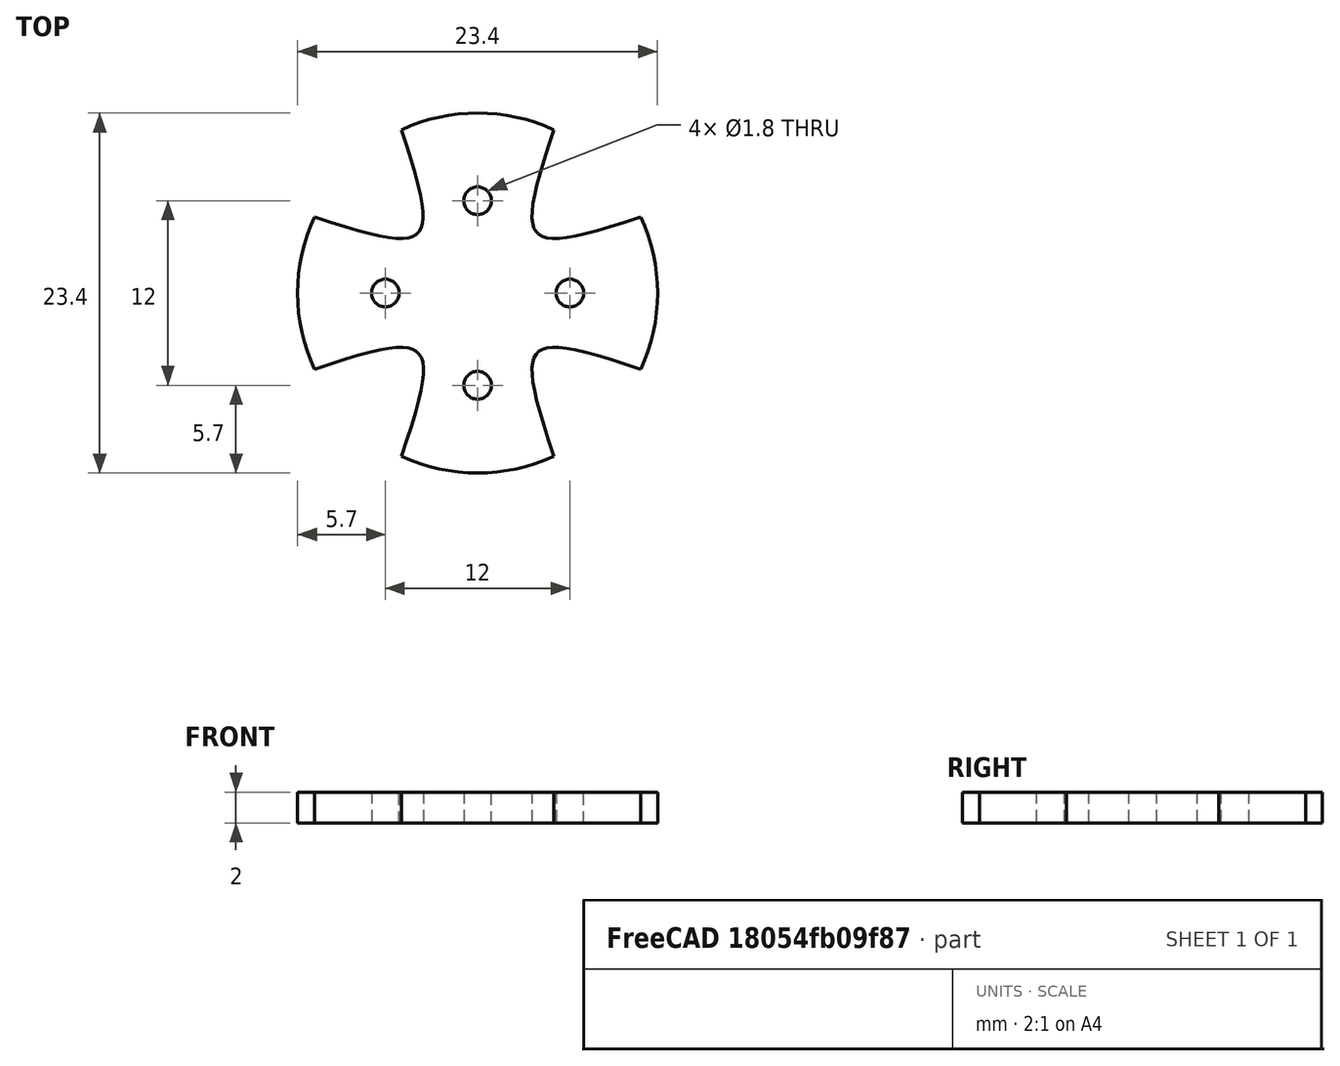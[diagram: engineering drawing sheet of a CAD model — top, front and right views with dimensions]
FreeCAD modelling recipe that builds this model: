
FCSTD DOCUMENT  (FreeCAD 0.19R0.19.2)
Label: boatMoterHolder011
License: All rights reserved
LicenseURL: http://en.wikipedia.org/wiki/All_rights_reserved
objects: Sketcher::SketchObject×2, Part::Extrusion×1
note: 3 computed .brp shape members not serialized (recipe doc carries the construction recipe); baked Part::Feature solids carry a one-line shape summary decoded from their .brp

FEATURE [Sketcher::SketchObject] Sketch
  FullyConstrained = true
  sketch-geometry (44):
    g0: Circle CenterX=-6 CenterY=0 CenterZ=0 NormalX=0 NormalY=0 NormalZ=1 AngleXU=0 Radius=0.9
    g1: Circle CenterX=0 CenterY=6 CenterZ=0 NormalX=0 NormalY=0 NormalZ=1 AngleXU=0 Radius=0.9
    g2: Circle CenterX=6 CenterY=0 CenterZ=0 NormalX=0 NormalY=0 NormalZ=1 AngleXU=0 Radius=0.9
    g3: Circle CenterX=0 CenterY=-6 CenterZ=0 NormalX=0 NormalY=0 NormalZ=1 AngleXU=0 Radius=0.9
    g4-g8: Circle x5 (B-spline internal-alignment scaffolding for g9; pole/knot coordinates omitted)
    g9: BSplineCurve PolesCount=5 KnotsCount=3 Degree=3 IsPeriodic=0
    g10: GeomPoint X=-4.94974 Y=10.6066 Z=0
    g11: GeomPoint X=-3.88908 Y=3.88909 Z=0
    g12: GeomPoint X=-10.6066 Y=4.94975 Z=0
    g13-g17: Circle x5 (B-spline internal-alignment scaffolding for g18; pole/knot coordinates omitted)
    g18: BSplineCurve PolesCount=5 KnotsCount=3 Degree=3 IsPeriodic=0
    g19: GeomPoint X=-10.6066 Y=-4.94974 Z=0
    g20: GeomPoint X=-3.88212 Y=-3.88197 Z=0
    g21: GeomPoint X=-4.94053 Y=-10.6109 Z=0
    g22-g26: Circle x5 (B-spline internal-alignment scaffolding for g27; pole/knot coordinates omitted)
    g27: BSplineCurve PolesCount=5 KnotsCount=3 Degree=3 IsPeriodic=0
    g28: GeomPoint X=4.94975 Y=-10.6066 Z=0
    g29: GeomPoint X=3.8852 Y=-3.88525 Z=0
    g30: GeomPoint X=10.603 Y=-4.95737 Z=0
    g31-g35: Circle x5 (B-spline internal-alignment scaffolding for g36; pole/knot coordinates omitted)
    g36: BSplineCurve PolesCount=5 KnotsCount=3 Degree=3 IsPeriodic=0
    g37: GeomPoint X=10.6066 Y=4.94975 Z=0
    g38: GeomPoint X=3.8891 Y=3.88908 Z=0
    g39: GeomPoint X=4.94975 Y=10.6066 Z=0
    g40: ArcOfCircle CenterX=0 CenterY=0 CenterZ=0 NormalX=0 NormalY=0 NormalZ=1 AngleXU=0 Radius=11.7047 StartAngle=1.13417 EndAngle=2.00742
    g41: ArcOfCircle CenterX=0 CenterY=0 CenterZ=0 NormalX=0 NormalY=0 NormalZ=1 AngleXU=0 Radius=11.7047 StartAngle=5.84584 EndAngle=6.71981
    g42: ArcOfCircle CenterX=0 CenterY=0 CenterZ=0 NormalX=0 NormalY=0 NormalZ=1 AngleXU=0 Radius=11.7047 StartAngle=4.27663 EndAngle=5.14902
    g43: ArcOfCircle CenterX=0 CenterY=0 CenterZ=0 NormalX=0 NormalY=0 NormalZ=1 AngleXU=0 Radius=11.7047 StartAngle=2.70497 EndAngle=3.57822
  constraints (50):
    c: Block(g1)
    c: Block(g2)
    c: Block(g3)
    c: Block(g0)
    c: Weight(g4) = 1
    c: Equal(g4, g5-g8) x4
    c: InternalAlignment(g4-g8 -> g9) x5
    c: InternalAlignment(g10,g9)
    c: InternalAlignment(g11,g9)
    c: InternalAlignment(g12,g9)
    c: Weight(g13) = 1
    c: Equal(g13, g14-g17) x4
    c: InternalAlignment(g13-g17 -> g18) x5
    c: InternalAlignment(g19,g18)
    c: InternalAlignment(g20,g18)
    c: InternalAlignment(g21,g18)
    c: Weight(g22) = 1
    c: Equal(g22,g24)
    c: Equal(g22,g25)
    c: Equal(g22,g26)
    c: InternalAlignment(g22-g26 -> g27) x5
    c: InternalAlignment(g28,g27)
    c: InternalAlignment(g29,g27)
    c: InternalAlignment(g30,g27)
    c: Weight(g31) = 1
    c: Equal(g31, g32-g35) x4
    c: InternalAlignment(g31-g35 -> g36) x5
    c: InternalAlignment(g37,g36)
    c: InternalAlignment(g38,g36)
    c: InternalAlignment(g39,g36)
    c: Coincident(g40,g-1)
    c: Coincident(g40,g9)
    c: Coincident(g40,g36)
    c: Coincident(g41,g40)
    c: Coincident(g41,g36)
    c: Coincident(g41,g27)
    c: Coincident(g42,g40)
    c: Coincident(g42,g27)
    c: Coincident(g42,g18)
    c: Coincident(g43,g40)
    c: Coincident(g43,g18)
    c: Coincident(g43,g9)
    c: Block(g41)
    c: Block(g40)
    c: Block(g43)
    c: Block(g42)
    c: Block(g36)
    c: Block(g9)
    c: Block(g27)
    c: Block(g18)
FEATURE [Part::Extrusion] Extrude
  Base = -> Sketch
  Dir = (0,0,1)
  DirMode = 2
  FaceMakerClass = Part::FaceMakerBullseye
  LengthFwd = 2
  LengthRev = 0
  Solid = true
  Symmetric = false
FEATURE [Sketcher::SketchObject] Sketch001
  FullyConstrained = true
  sketch-geometry (44):
    g0: ArcOfCircle CenterX=0 CenterY=0 CenterZ=0 NormalX=0 NormalY=0 NormalZ=1 AngleXU=0 Radius=11.7047 StartAngle=1.13417 EndAngle=1.50239
    g1: ArcOfCircle CenterX=0 CenterY=0 CenterZ=0 NormalX=0 NormalY=0 NormalZ=1 AngleXU=0 Radius=11.7047 StartAngle=5.84584 EndAngle=6.21478
    g2: ArcOfCircle CenterX=0 CenterY=0 CenterZ=0 NormalX=0 NormalY=0 NormalZ=1 AngleXU=0 Radius=11.7047 StartAngle=4.27663 EndAngle=4.64399
    g3: ArcOfCircle CenterX=0 CenterY=0 CenterZ=0 NormalX=0 NormalY=0 NormalZ=1 AngleXU=0 Radius=11.7047 StartAngle=2.70497 EndAngle=3.07319
    g4: LineSegment StartX=22.4 StartY=-0.8 StartZ=0 EndX=11.6773 EndY=-0.8 EndZ=0
    g5: LineSegment StartX=22.4 StartY=0.8 StartZ=0 EndX=11.6773 EndY=0.8 EndZ=0
    g6: LineSegment StartX=0.8 StartY=22.4 StartZ=0 EndX=0.8 EndY=11.6773 EndZ=0
    g7: LineSegment StartX=-0.8 StartY=22.4 StartZ=0 EndX=-0.8 EndY=11.6773 EndZ=0
    g8: LineSegment StartX=-22.4 StartY=0.8 StartZ=0 EndX=-11.6773 EndY=0.8 EndZ=0
    g9: LineSegment StartX=-22.4 StartY=-0.8 StartZ=0 EndX=-11.6773 EndY=-0.8 EndZ=0
    g10: LineSegment StartX=-22.4 StartY=0.8 StartZ=0 EndX=-22.4 EndY=-0.8 EndZ=0
    g11: ArcOfCircle CenterX=0 CenterY=0 CenterZ=0 NormalX=0 NormalY=0 NormalZ=1 AngleXU=0 Radius=11.7047 StartAngle=3.20999 EndAngle=3.57822
    g12: ArcOfCircle CenterX=0 CenterY=0 CenterZ=0 NormalX=0 NormalY=0 NormalZ=1 AngleXU=0 Radius=11.7047 StartAngle=1.6392 EndAngle=2.00742
    g13: ArcOfCircle CenterX=0 CenterY=0 CenterZ=0 NormalX=0 NormalY=0 NormalZ=1 AngleXU=0 Radius=11.7047 StartAngle=0.0684019 EndAngle=0.436627
    g14: LineSegment StartX=-0.8 StartY=22.4 StartZ=0 EndX=0.8 EndY=22.4 EndZ=0
    g15: LineSegment StartX=22.4 StartY=-0.8 StartZ=0 EndX=22.4 EndY=0.8 EndZ=0
    g16: LineSegment StartX=0.8 StartY=-22.4 StartZ=0 EndX=0.8 EndY=-11.6773 EndZ=0
    g17: LineSegment StartX=-0.8 StartY=-22.4 StartZ=0 EndX=-0.8 EndY=-11.6773 EndZ=0
    g18: LineSegment StartX=-0.8 StartY=-22.4 StartZ=0 EndX=0.8 EndY=-22.4 EndZ=0
    g19: ArcOfCircle CenterX=0 CenterY=0 CenterZ=0 NormalX=0 NormalY=0 NormalZ=1 AngleXU=0 Radius=11.7047 StartAngle=4.78079 EndAngle=5.14902
    g20: Circle CenterX=-10.6066 CenterY=4.94975 CenterZ=0 NormalX=0 NormalY=0 NormalZ=1 AngleXU=0 Radius=1
    g21: Circle CenterX=-8.2 CenterY=0 CenterZ=0 NormalX=0 NormalY=0 NormalZ=1 AngleXU=0 Radius=1
    g22: Circle CenterX=-10.6066 CenterY=-4.94974 CenterZ=0 NormalX=0 NormalY=0 NormalZ=1 AngleXU=0 Radius=1
    g23: BSplineCurve PolesCount=3 KnotsCount=2 Degree=2 IsPeriodic=0
    g24: GeomPoint X=-10.6066 Y=4.94975 Z=0
    g25: GeomPoint X=-10.6066 Y=-4.94974 Z=0
    g26: Circle CenterX=-4.94974 CenterY=10.6066 CenterZ=0 NormalX=0 NormalY=0 NormalZ=1 AngleXU=0 Radius=1
    g27: Circle CenterX=0 CenterY=8.2 CenterZ=0 NormalX=0 NormalY=0 NormalZ=1 AngleXU=0 Radius=1
    g28: Circle CenterX=4.94975 CenterY=10.6066 CenterZ=0 NormalX=0 NormalY=0 NormalZ=1 AngleXU=0 Radius=1
    g29: BSplineCurve PolesCount=3 KnotsCount=2 Degree=2 IsPeriodic=0
    g30: GeomPoint X=-4.94974 Y=10.6066 Z=0
    g31: GeomPoint X=4.94975 Y=10.6066 Z=0
    g32: Circle CenterX=10.6066 CenterY=4.94975 CenterZ=0 NormalX=0 NormalY=0 NormalZ=1 AngleXU=0 Radius=1
    g33: Circle CenterX=8.2 CenterY=0 CenterZ=0 NormalX=0 NormalY=0 NormalZ=1 AngleXU=0 Radius=1
    g34: Circle CenterX=10.603 CenterY=-4.95737 CenterZ=0 NormalX=0 NormalY=0 NormalZ=1 AngleXU=0 Radius=1
    g35: BSplineCurve PolesCount=3 KnotsCount=2 Degree=2 IsPeriodic=0
    g36: GeomPoint X=10.6066 Y=4.94975 Z=0
    g37: GeomPoint X=10.603 Y=-4.95737 Z=0
    g38: Circle CenterX=4.94975 CenterY=-10.6066 CenterZ=0 NormalX=0 NormalY=0 NormalZ=1 AngleXU=0 Radius=1
    g39: Circle CenterX=0 CenterY=-8.2 CenterZ=0 NormalX=0 NormalY=0 NormalZ=1 AngleXU=0 Radius=1
    g40: Circle CenterX=-4.94053 CenterY=-10.6109 CenterZ=0 NormalX=0 NormalY=0 NormalZ=1 AngleXU=0 Radius=1
    g41: BSplineCurve PolesCount=3 KnotsCount=2 Degree=2 IsPeriodic=0
    g42: GeomPoint X=4.94975 Y=-10.6066 Z=0
    g43: GeomPoint X=-4.94053 Y=-10.6109 Z=0
  constraints (106):
    c: Coincident(g0,g-1)
    c: Coincident(g1,g0)
    c: Coincident(g2,g0)
    c: Coincident(g3,g0)
    c: Block(g1)
    c: Block(g0)
    c: Block(g3)
    c: Block(g2)
    c: Horizontal(g4)
    c: Horizontal(g5)
    c: Vertical(g6)
    c: Vertical(g7)
    c: Horizontal(g8)
    c: Horizontal(g9)
    c: Block(g9)
    c: Block(g8)
    c: Block(g7)
    c: Block(g6)
    c: Block(g5)
    c: Block(g4)
    c: Coincident(g10,g8)
    c: Coincident(g10,g9)
    c: Vertical(g10)
    c: Distance(g10) = 1.6
    c: Equal(g3,g11)
    c: Coincident(g3,g8)
    c: Coincident(g11,g9)
    c: Coincident(g3,g11)
    c: Equal(g0,g12)
    c: Coincident(g0,g6)
    c: Coincident(g12,g7)
    c: Coincident(g0,g12)
    c: Equal(g1,g13)
    c: Coincident(g1,g4)
    c: PointOnObject(g13,g5)
    c: Coincident(g1,g13)
    c: Coincident(g14,g7)
    c: Coincident(g14,g6)
    c: Horizontal(g14)
    c: Distance(g14) = 1.6
    c: Coincident(g15,g4)
    c: Coincident(g15,g5)
    c: Vertical(g15)
    c: Distance(g15) = 1.6
    c: Vertical(g16)
    c: Vertical(g17)
    c: Block(g16)
    c: Block(g17)
    c: Coincident(g18,g17)
    c: Coincident(g18,g16)
    c: Horizontal(g18)
    c: Equal(g2,g19)
    c: Coincident(g2,g17)
    c: Coincident(g19,g16)
    c: Coincident(g2,g19)
    c: Block(g11)
    c: Block(g12)
    c: Block(g13)
    c: Block(g19)
    c: PointOnObject(g21,g-1)
    c: PointOnObject(g33,g-1)
    c: PointOnObject(g39,g-2)
    c: Coincident(g23,g3)
    c: Weight(g20) = 1
    c: Equal(g20,g21)
    c: Equal(g20,g22)
    c: Coincident(g23,g11)
    c: InternalAlignment(g20,g23)
    c: InternalAlignment(g21,g23)
    c: InternalAlignment(g22,g23)
    c: InternalAlignment(g24,g23)
    c: InternalAlignment(g25,g23)
    c: Coincident(g29,g12)
    c: Weight(g26) = 1
    c: Equal(g26,g27)
    c: Equal(g26,g28)
    c: Coincident(g29,g0)
    c: InternalAlignment(g26,g29)
    c: InternalAlignment(g27,g29)
    c: InternalAlignment(g28,g29)
    c: InternalAlignment(g30,g29)
    c: InternalAlignment(g31,g29)
    c: Coincident(g35,g13)
    c: Weight(g32) = 1
    c: Equal(g32,g33)
    c: Equal(g32,g34)
    c: Coincident(g35,g1)
    c: InternalAlignment(g32,g35)
    c: InternalAlignment(g33,g35)
    c: InternalAlignment(g34,g35)
    c: InternalAlignment(g36,g35)
    c: InternalAlignment(g37,g35)
    c: Coincident(g41,g19)
    c: Weight(g38) = 1
    c: Equal(g38,g39)
    c: Equal(g38,g40)
    c: Coincident(g41,g2)
    c: InternalAlignment(g38,g41)
    c: InternalAlignment(g39,g41)
    c: InternalAlignment(g40,g41)
    c: InternalAlignment(g42,g41)
    c: InternalAlignment(g43,g41)
    c: Block(g29)
    c: Block(g23)
    c: Block(g35)
    c: Block(g41)
